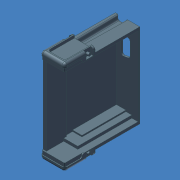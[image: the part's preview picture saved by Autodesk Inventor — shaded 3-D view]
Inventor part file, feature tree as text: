
AUTODESK INVENTOR PART (.ipt)
format: ipt  version: unknown  size: 482,304 bytes
history: native  units: mm (DEFAULTED — no unit token found)
features: sketch x15, extrude x14, fillet x5, mirror x4, other x1
ambient origin geometry x8: Origin, YZ Plane, XZ Plane, XY Plane, X Axis, Y Axis, Z Axis, Center Point
feature tree (39):
  extrude  "Extrusion1"  Depth=88.1888mm
  extrude  "Extrusion2"  Depth=41.91mm
  mirror  "Mirror1"
  extrude  "Extrusion3"  Depth=25.4mm TaperAngle=0.0deg
  extrude  "Extrusion4"  Depth=1.5748mm
  extrude  "Extrusion5"  Depth=19.05mm TaperAngle=0.0deg
  extrude  "Extrusion6"  Depth=3.81mm
  extrude  "Extrusion7"  Depth=16.51mm
  extrude  "Extrusion8"  Depth=0.7874mm TaperAngle=0.0deg
  fillet  "Fillet1"  Radius=0.7874mm
  fillet  "Fillet2"  Radius=1.27mm
  extrude  "Extrusion9"  Depth=1.778mm
  fillet  "Fillet3"  Radius=48.26mm
  extrude  "Extrusion10"  Depth=3.556mm
  mirror  "Mirror2"
  mirror  "Mirror3"
  extrude  "Extrusion11"  Depth=7.62mm
  extrude  "Extrusion12"  Depth=20.32mm
  mirror  "Mirror4"
  fillet  "Fillet4"  Radius=6.604mm
  extrude  "Extrusion14"  Depth=2.54mm
  extrude  "Extrusion15"  Depth=2.54mm TaperAngle=0.0deg
  fillet  "Fillet5"  Radius=14.478mm
  sketch  "Sketch1"  dims[d0=22.86mm d1=88.1888mm]
  sketch  "Sketch3"  dims[d2=70.612mm d3=0.0mm d6=41.91mm]
  sketch  "Sketch4"  dims[d7=4.572mm d8=25.4mm d9=0.0mm]
  sketch  "Sketch5"  dims[d10=2.54mm d11=1.5748mm]
  sketch  "Sketch6"  dims[d12=2.54mm d13=19.05mm d14=0.0mm]
  sketch  "Sketch9"  dims[d15=1.27mm d16=0.0mm d17=3.81mm]
  sketch  "Sketch10"  dims[d18=3.81mm d19=16.51mm]
  sketch  "Sketch11"  dims[d20=0.7874mm d21=0.0mm d22=0.7874mm d23=0.0mm d24=0.7874mm d25=0.0mm d26=1.27mm d27=0.0mm]
  sketch  "Sketch12"  dims[d28=0.7874mm d29=1.778mm d30=48.26mm]
  sketch  "Sketch13"  dims[d32=16.002mm d33=3.556mm]
  sketch  "Sketch14"  dims[d34=2.54mm d35=0.0mm d36=7.62mm]
  sketch  "Sketch15"  dims[d38=2.54mm d39=20.32mm d40=6.604mm]
  sketch  "Sketch18"  dims[d41=6.35mm d42=2.54mm]
  sketch  "Sketch19"  dims[d43=2.54mm d44=2.54mm d45=0.0mm d46=14.478mm]
  sketch  "Sketch20"  dims[d47=50.8mm d48=2.54mm d49=0.0mm d51=8.89mm d52=41.275mm d53=1.27mm d54=0.0mm d55=2.54mm d63=7.312076mm d64=3.175mm d65=15.53343mm d66=15.53343mm d67=3.81mm d68=0.0mm d69=15.53343mm d70=3.175mm d71=15.53343mm d72=6.35mm d73=3.81mm d74=0.0mm d75=1.27mm d77=18.542mm d85=-15.707963mm]
  other  "iFeature10:1"
